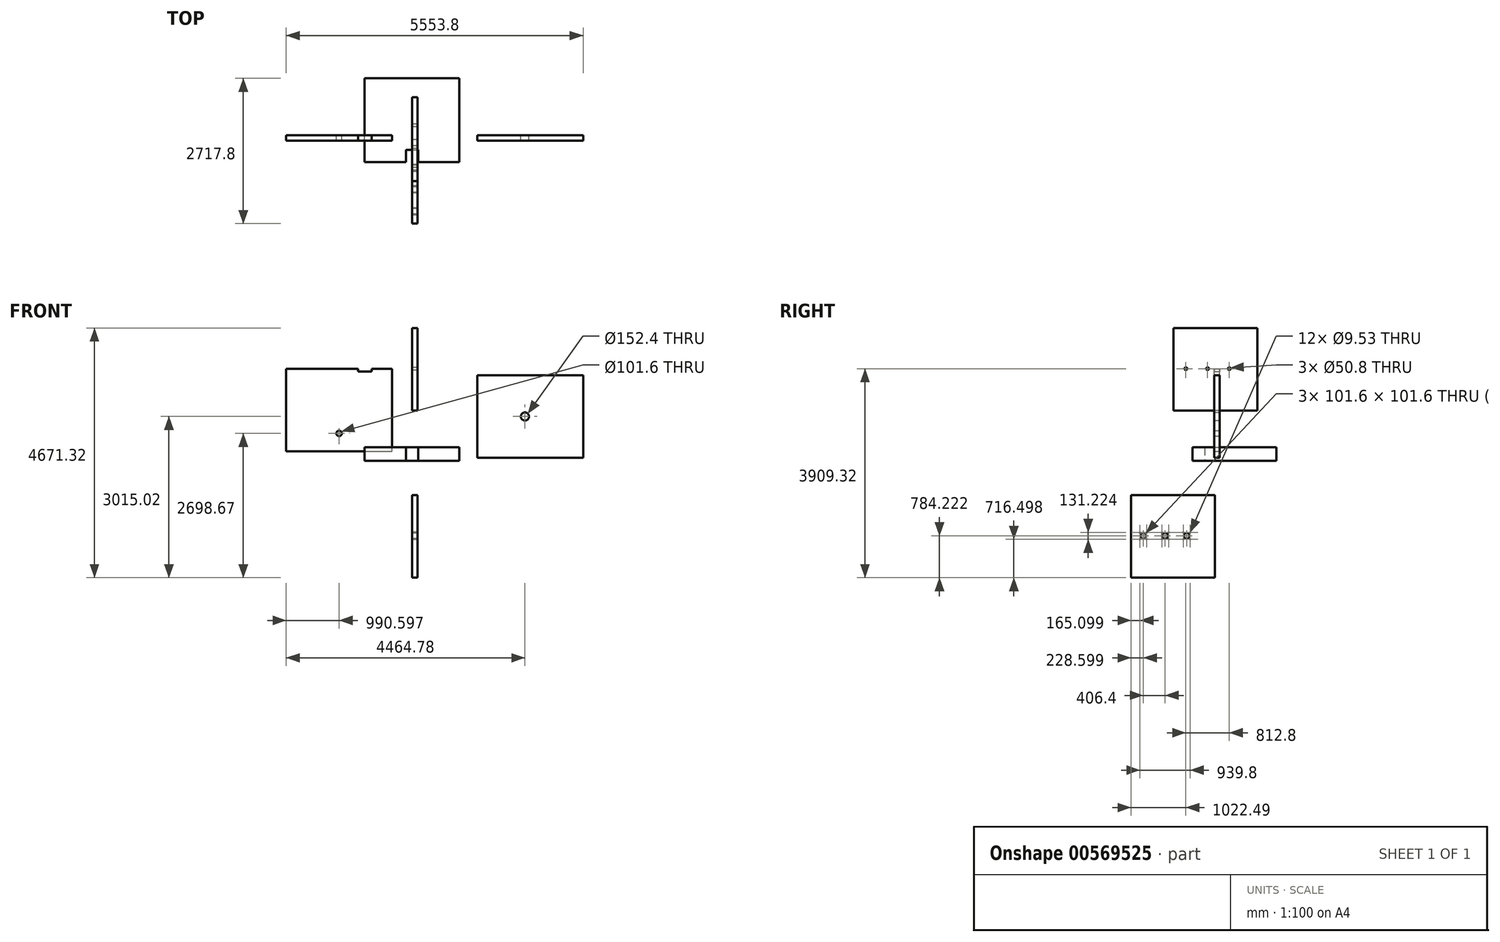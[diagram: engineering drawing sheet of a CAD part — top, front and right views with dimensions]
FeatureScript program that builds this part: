
annotation { "Feature Type Name" : "Feature", "Feature Type Description" : "" }
export const myFeature = defineFeature(function(context is Context, id is Id, definition is map)
    precondition{}
    {
        {
            var Q0;
            Q0=qCreatedBy(makeId("Top.planeOp"),FACE);
            var sketch = newSketch(context, id + "F0", { "sketchPlane" : qUnion([Q0])});
            skLineSegment(sketch, "E0.bottom", {"start": v(-885.83, -505.86) * mm, "end": v(885.82, -505.86) * mm});
            skLineSegment(sketch, "E0.top", {"start": v(-885.83, 1062.6) * mm, "end": v(885.82, 1062.6) * mm});
            skLineSegment(sketch, "E0.left", {"start": v(-885.83, -505.86) * mm, "end": v(-885.83, 1062.6) * mm});
            skLineSegment(sketch, "E0.right", {"start": v(885.83, -505.86) * mm, "end": v(885.82, 1062.6) * mm});
            skLineSegment(sketch, "E1.bottom", {"start": v(-114.3, -505.86) * mm, "end": v(114.3, -505.86) * mm});
            skLineSegment(sketch, "E1.top", {"start": v(-114.3, -277.26) * mm, "end": v(114.3, -277.26) * mm});
            skLineSegment(sketch, "E1.left", {"start": v(-114.3, -505.86) * mm, "end": v(-114.3, -277.26) * mm});
            skLineSegment(sketch, "E1.right", {"start": v(114.3, -505.86) * mm, "end": v(114.3, -277.26) * mm});
            skSolve(sketch);
        }
        {
            var Q0;
            Q0=qCreatedBy(makeId("Right.planeOp"),FACE);
            var sketch = newSketch(context, id + "F1", { "sketchPlane" : qUnion([Q0])});
            skLineSegment(sketch, "E2.bottom", {"start": v(707.13, 940.17) * mm, "end": v(-861.32, 940.17) * mm});
            skLineSegment(sketch, "E2.top", {"start": v(707.13, 2486.4) * mm, "end": v(-861.32, 2486.4) * mm});
            skLineSegment(sketch, "E2.left", {"start": v(707.13, 940.17) * mm, "end": v(707.13, 2486.4) * mm});
            skLineSegment(sketch, "E2.right", {"start": v(-861.32, 940.17) * mm, "end": v(-861.32, 2486.4) * mm});
            skCircle(sketch, "E3", {"center": v(180.08, 1724.4) * mm, "radius": 25.4 * mm});
            skCircle(sketch, "E4", {"center": v(-226.32, 1724.4) * mm, "radius": 25.4 * mm});
            skCircle(sketch, "E5", {"center": v(-632.72, 1724.4) * mm, "radius": 25.4 * mm});
            skSolve(sketch);
        }
        {
            var Q0;
            Q0=qCreatedBy(makeId("Right.planeOp"),FACE);
            var sketch = newSketch(context, id + "F2", { "sketchPlane" : qUnion([Q0])});
            skLineSegment(sketch, "E6.bottom", {"start": v(-1655.21, -2184.93) * mm, "end": v(-86.76, -2184.93) * mm});
            skLineSegment(sketch, "E6.top", {"start": v(-1655.21, -638.7) * mm, "end": v(-86.76, -638.7) * mm});
            skLineSegment(sketch, "E6.left", {"start": v(-1655.21, -2184.93) * mm, "end": v(-1655.21, -638.7) * mm});
            skLineSegment(sketch, "E6.right", {"start": v(-86.76, -2184.93) * mm, "end": v(-86.76, -638.7) * mm});
            skLineSegment(sketch, "E7.bottom", {"start": v(-1477.41, -1451.5) * mm, "end": v(-1375.81, -1451.5) * mm});
            skLineSegment(sketch, "E7.top", {"start": v(-1477.41, -1349.9) * mm, "end": v(-1375.81, -1349.9) * mm});
            skLineSegment(sketch, "E7.left", {"start": v(-1477.41, -1451.5) * mm, "end": v(-1477.41, -1349.9) * mm});
            skLineSegment(sketch, "E7.right", {"start": v(-1375.81, -1451.5) * mm, "end": v(-1375.81, -1349.9) * mm});
            skLineSegment(sketch, "E8.bottom", {"start": v(-1071.01, -1349.9) * mm, "end": v(-969.41, -1349.9) * mm});
            skLineSegment(sketch, "E8.top", {"start": v(-1071.01, -1451.5) * mm, "end": v(-969.41, -1451.5) * mm});
            skLineSegment(sketch, "E8.left", {"start": v(-1071.01, -1349.9) * mm, "end": v(-1071.01, -1451.5) * mm});
            skLineSegment(sketch, "E8.right", {"start": v(-969.41, -1349.9) * mm, "end": v(-969.41, -1451.5) * mm});
            skLineSegment(sketch, "E9.bottom", {"start": v(-664.61, -1349.9) * mm, "end": v(-563.01, -1349.9) * mm});
            skLineSegment(sketch, "E9.top", {"start": v(-664.61, -1451.5) * mm, "end": v(-563.01, -1451.5) * mm});
            skLineSegment(sketch, "E9.left", {"start": v(-664.61, -1349.9) * mm, "end": v(-664.61, -1451.5) * mm});
            skLineSegment(sketch, "E9.right", {"start": v(-563.01, -1349.9) * mm, "end": v(-563.01, -1451.5) * mm});
            skCircle(sketch, "E10", {"center": v(-1363.11, -1337.2) * mm, "radius": 4.76 * mm});
            skCircle(sketch, "E11", {"center": v(-1490.11, -1468.43) * mm, "radius": 4.76 * mm});
            skCircle(sketch, "E12", {"center": v(-1490.11, -1341.43) * mm, "radius": 4.76 * mm});
            skCircle(sketch, "E13", {"center": v(-1363.11, -1464.2) * mm, "radius": 4.76 * mm});
            skCircle(sketch, "E14", {"center": v(-1078.95, -1337.2) * mm, "radius": 4.76 * mm});
            skCircle(sketch, "E15", {"center": v(-951.95, -1337.2) * mm, "radius": 4.76 * mm});
            skCircle(sketch, "E16", {"center": v(-951.95, -1464.2) * mm, "radius": 4.76 * mm});
            skCircle(sketch, "E17", {"center": v(-1078.95, -1464.2) * mm, "radius": 4.76 * mm});
            skCircle(sketch, "E18", {"center": v(-677.31, -1337.2) * mm, "radius": 4.76 * mm});
            skCircle(sketch, "E19", {"center": v(-550.31, -1337.2) * mm, "radius": 4.76 * mm});
            skCircle(sketch, "E20", {"center": v(-550.31, -1464.2) * mm, "radius": 4.76 * mm});
            skCircle(sketch, "E21", {"center": v(-677.31, -1464.2) * mm, "radius": 4.76 * mm});
            skSolve(sketch);
        }
        {
            var Q0;
            Q0=qCreatedBy(makeId("Front.planeOp"),FACE);
            var sketch = newSketch(context, id + "F3", { "sketchPlane" : qUnion([Q0])});
            skLineSegment(sketch, "E22.bottom", {"start": v(-2353.05, 176.56) * mm, "end": v(-371.85, 176.56) * mm});
            skLineSegment(sketch, "E22.top", {"start": v(-2353.05, 1722.78) * mm, "end": v(-371.85, 1722.78) * mm});
            skLineSegment(sketch, "E22.left", {"start": v(-2353.05, 176.56) * mm, "end": v(-2353.05, 1722.78) * mm});
            skLineSegment(sketch, "E22.right", {"start": v(-371.85, 176.56) * mm, "end": v(-371.85, 1722.78) * mm});
            skLineSegment(sketch, "E23.bottom", {"start": v(-1006.85, 1722.78) * mm, "end": v(-752.85, 1722.78) * mm});
            skLineSegment(sketch, "E23.top", {"start": v(-1006.85, 1671.98) * mm, "end": v(-752.85, 1671.98) * mm});
            skLineSegment(sketch, "E23.left", {"start": v(-1006.85, 1722.78) * mm, "end": v(-1006.85, 1671.98) * mm});
            skLineSegment(sketch, "E23.right", {"start": v(-752.85, 1722.78) * mm, "end": v(-752.85, 1671.98) * mm});
            skCircle(sketch, "E24", {"center": v(-1362.45, 513.74) * mm, "radius": 50.8 * mm});
            skSolve(sketch);
        }
        {
            var Q0;
            Q0=qCreatedBy(makeId("Front.planeOp"),FACE);
            var sketch = newSketch(context, id + "F4", { "sketchPlane" : qUnion([Q0])});
            skLineSegment(sketch, "E25.bottom", {"start": v(1219.55, 55.39) * mm, "end": v(3200.75, 55.39) * mm});
            skLineSegment(sketch, "E25.top", {"start": v(1219.55, 1601.61) * mm, "end": v(3200.75, 1601.61) * mm});
            skLineSegment(sketch, "E25.left", {"start": v(1219.55, 55.39) * mm, "end": v(1219.55, 1601.61) * mm});
            skLineSegment(sketch, "E25.right", {"start": v(3200.75, 55.39) * mm, "end": v(3200.75, 1601.61) * mm});
            skCircle(sketch, "E26", {"center": v(2111.73, 830.09) * mm, "radius": 76.2 * mm});
            skSolve(sketch);
        }
        {
            var Q0;
            Q0=makeQuery(id+"F3.imprint","IMPRINT",FACE,{"disambiguationData":[TD([[makeQuery(id+"F3.imprint","IMPRINT",EDGE,{"derivedFrom":sQuery(id+"F3.wireOp",EDGE,"E22.bottom")}),1.0]])]});
            extrude(context, id + "F5", {"entities" : qUnion([Q0]), "depth" : 101.6 * mm, "offsetDistance" : 25.4 * mm});
        }
        {
            var Q0;
            Q0=makeQuery(id+"F4.imprint","IMPRINT",FACE,{"disambiguationData":[TD([[makeQuery(id+"F4.imprint","IMPRINT",EDGE,{"derivedFrom":sQuery(id+"F4.wireOp",EDGE,"E25.bottom")}),1.0]])]});
            extrude(context, id + "F6", {"entities" : qUnion([Q0]), "depth" : 101.6 * mm, "offsetDistance" : 25.4 * mm});
        }
        {
            var Q0;
            Q0=makeQuery(id+"F1.imprint","IMPRINT",FACE,{"disambiguationData":[TD([[makeQuery(id+"F1.imprint","IMPRINT",EDGE,{"derivedFrom":sQuery(id+"F1.wireOp",EDGE,"E2.bottom")}),-1.0]])]});
            extrude(context, id + "F7", {"entities" : qUnion([Q0]), "depth" : 101.6 * mm, "offsetDistance" : 25.4 * mm});
        }
        {
            var Q0;
            Q0=makeQuery(id+"F0.imprint","IMPRINT",FACE,{"disambiguationData":[TD([[makeQuery(id+"F0.imprint","IMPRINT",EDGE,{"derivedFrom":sQuery(id+"F0.wireOp",EDGE,"E0.bottom")}),1.0]])]});
            extrude(context, id + "F8", {"entities" : qUnion([Q0]), "depth" : 254 * mm, "offsetDistance" : 25.4 * mm});
        }
        {
            var Q0;
            Q0=makeQuery(id+"F2.imprint","IMPRINT",FACE,{"disambiguationData":[TD([[makeQuery(id+"F2.imprint","IMPRINT",EDGE,{"derivedFrom":sQuery(id+"F2.wireOp",EDGE,"E6.bottom")}),1.0]])]});
            extrude(context, id + "F9", {"entities" : qUnion([Q0]), "depth" : 101.6 * mm, "offsetDistance" : 25.4 * mm});
        }
    });
